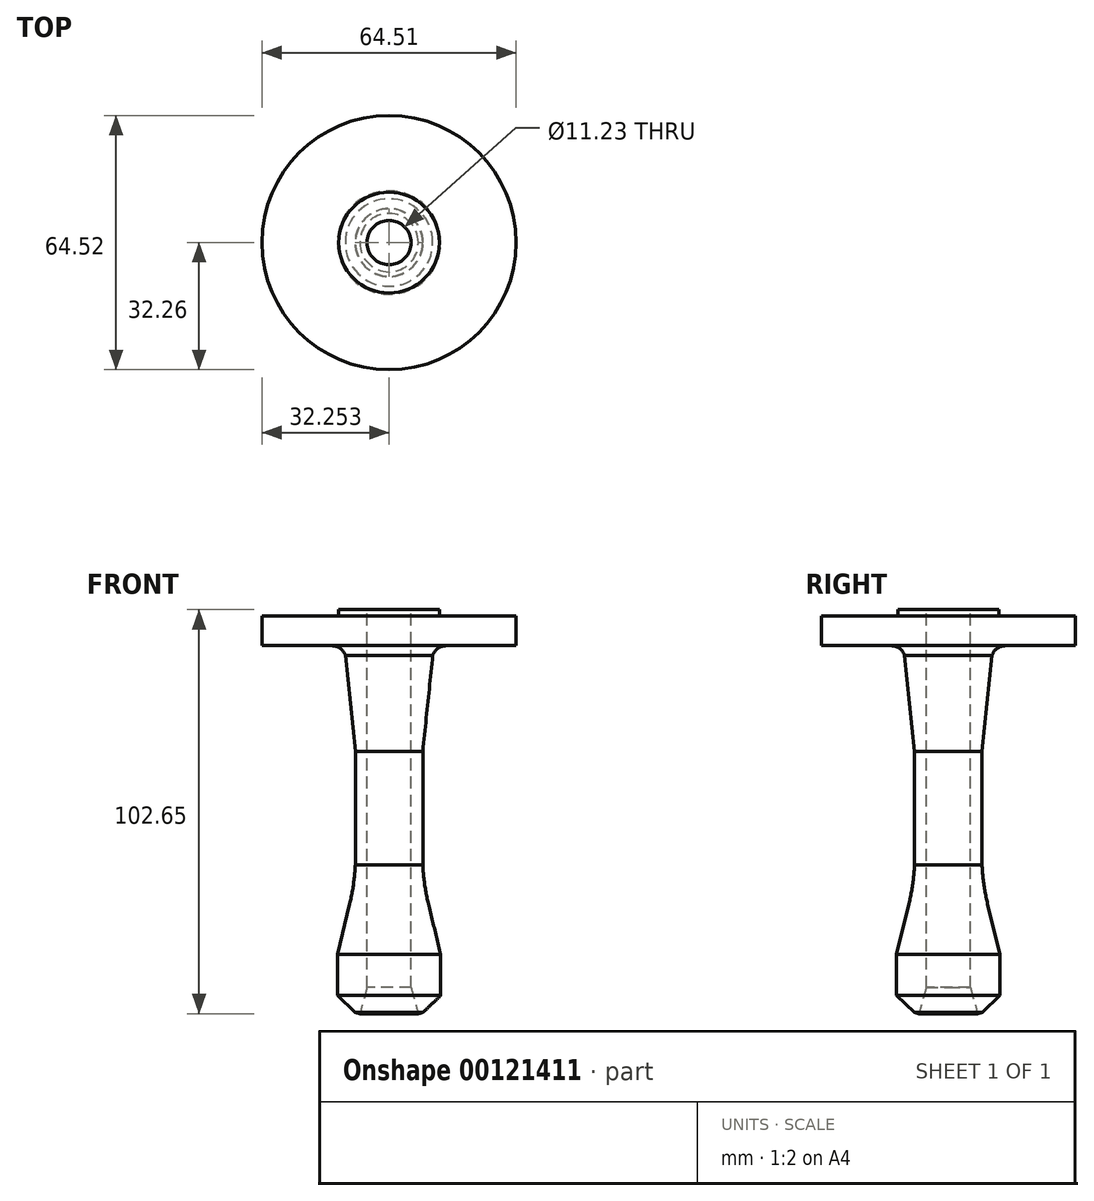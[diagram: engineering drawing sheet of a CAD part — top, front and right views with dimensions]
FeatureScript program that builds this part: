
annotation { "Feature Type Name" : "Feature", "Feature Type Description" : "" }
export const myFeature = defineFeature(function(context is Context, id is Id, definition is map)
    precondition{}
    {
        {
            var Q0;
            Q0=qCreatedBy(makeId("Front.planeOp"),FACE);
            var sketch = newSketch(context, id + "F0", { "sketchPlane" : qUnion([Q0])});
            skLineSegment(sketch, "E0", {"start": v(-12.72, 50.44) * mm, "end": v(-12.72, -45.46) * mm});
            skLineSegment(sketch, "E1", {"start": v(-12.72, -45.46) * mm, "end": v(-10.9, -52.08) * mm});
            skLineSegment(sketch, "E2", {"start": v(-10.9, -52.08) * mm, "end": v(-9.71, -51.76) * mm});
            skLineSegment(sketch, "E3", {"start": v(-9.71, -51.76) * mm, "end": v(-5.2, -47.48) * mm});
            skLineSegment(sketch, "E4", {"start": v(-5.2, -47.48) * mm, "end": v(-5.2, -37.06) * mm});
            skLineSegment(sketch, "E5", {"start": v(-5.2, -37.06) * mm, "end": v(-8.35, -24.13) * mm});
            skArc(sketch, "E6", {"start": v(-9.76, -14.24) * mm, "mid": v(-9.3, -19.22) * mm, "end": v(-8.35, -24.13) * mm});
            skLineSegment(sketch, "E7", {"start": v(-9.76, -14.24) * mm, "end": v(-9.76, 14.54) * mm});
            skLineSegment(sketch, "E8", {"start": v(-9.76, 14.54) * mm, "end": v(-7.23, 38.96) * mm});
            skLineSegment(sketch, "E9", {"start": v(13.92, 41.4) * mm, "end": v(-3.83, 41.4) * mm});
            skArc(sketch, "E10", {"start": v(-3.83, 41.4) * mm, "mid": v(-5.93, 40.73) * mm, "end": v(-7.23, 38.96) * mm});
            skLineSegment(sketch, "E11", {"start": v(13.92, 41.4) * mm, "end": v(13.92, 48.97) * mm});
            skLineSegment(sketch, "E12", {"start": v(13.92, 48.97) * mm, "end": v(-5.51, 48.97) * mm});
            skLineSegment(sketch, "E13", {"start": v(-5.51, 48.97) * mm, "end": v(-5.51, 50.57) * mm});
            skLineSegment(sketch, "E14", {"start": v(-5.51, 50.57) * mm, "end": v(-12.72, 50.44) * mm});
            skLineSegment(sketch, "E15", {"start": v(-18.34, 54.36) * mm, "end": v(-18.34, 44.03) * mm});
            skLineSegment(sketch, "E16", {"start": v(-18.34, 44.03) * mm, "end": v(-18.34, -59.47) * mm});
            skSolve(sketch);
        }
        {
            var Q0;
            Q0=makeQuery(id+"F0.imprint","IMPRINT",FACE,{"disambiguationData":[TD([[makeQuery(id+"F0.imprint","IMPRINT",EDGE,{"derivedFrom":sQuery(id+"F0.wireOp",EDGE,"E0")}),1.0]])]});
            var Q1;
            Q1=sQuery(id+"F0.wireOp",EDGE,"E16");
            revolve(context, id + "F1", {"entities" : qUnion([Q0]), "axis" : qUnion([Q1]), "revolveType" : RevolveType.FULL});
        }
    });
